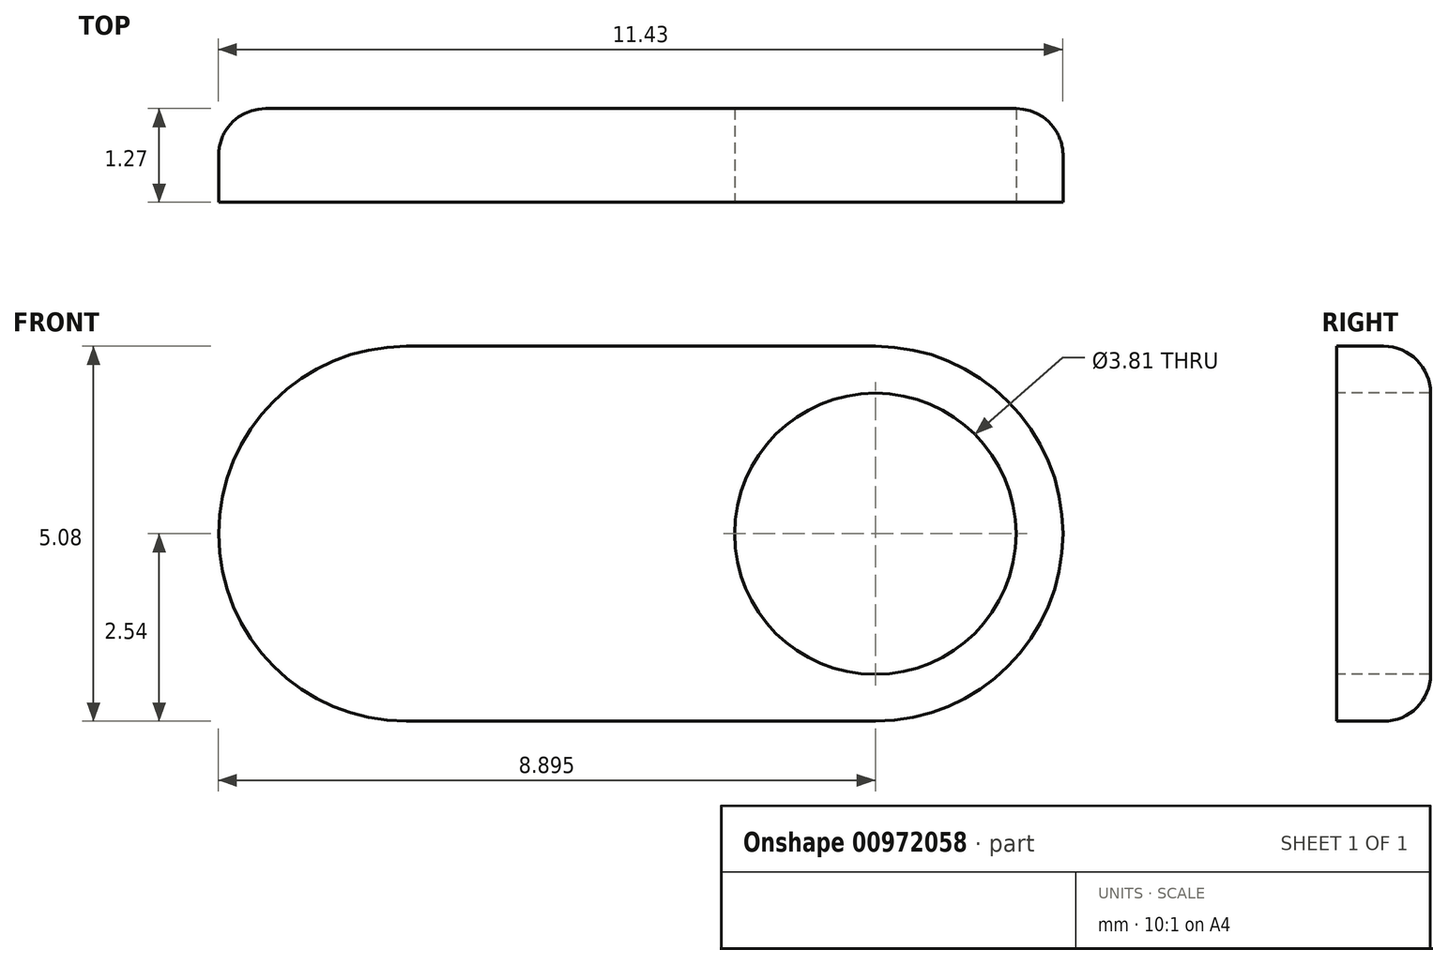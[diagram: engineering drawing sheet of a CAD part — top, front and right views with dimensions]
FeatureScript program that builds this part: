
annotation { "Feature Type Name" : "Feature", "Feature Type Description" : "" }
export const myFeature = defineFeature(function(context is Context, id is Id, definition is map)
    precondition{}
    {
        {
            var Q0;
            Q0=qCreatedBy(makeId("Front.planeOp"),FACE);
            var sketch = newSketch(context, id + "F0", { "sketchPlane" : qUnion([Q0])});
            skPoint(sketch, "E0", {"position": v(-3.17, 0) * mm});
            skPoint(sketch, "E1", {"position": v(3.18, 0) * mm});
            skCircle(sketch, "E2", {"center": v(-3.17, 0) * mm, "radius": 2.54 * mm});
            skCircle(sketch, "E3", {"center": v(3.18, 0) * mm, "radius": 2.54 * mm});
            skLineSegment(sketch, "E4", {"start": v(-3.18, 2.54) * mm, "end": v(3.18, 2.54) * mm});
            skLineSegment(sketch, "E5", {"start": v(-3.18, -2.54) * mm, "end": v(3.18, -2.54) * mm});
            skSolve(sketch);
        }
        {
            var Q0;
            Q0 = qSketchRegion(id + "F0", true);
            extrude(context, id + "F1", {"entities" : qUnion([Q0]), "depth" : 1.27 * mm, "offsetDistance" : 25.4 * mm});
        }
        {
            var Q0;
            Q0=makeQuery(id+"F1.opExtrude","CAP_EDGE",EDGE,{"disambiguationData":[OSD([sQuery(id+"F0.wireOp",EDGE,"E5")])],"isStart":true});
            fillet(context, id + "F2", {"entities" : qUnion([Q0]), "radius" : 0.64 * mm, "tangentPropagation" : true, "allowEdgeOverflow" : false});
        }
        {
            var Q0;
            Q0=makeQuery(id+"F1.opExtrude","CAP_FACE",FACE,{"disambiguationData":[OSD([sQuery(id+"F0.wireOp",EDGE,"E2"),sQuery(id+"F0.wireOp",EDGE,"E3"),sQuery(id+"F0.wireOp",EDGE,"E4"),sQuery(id+"F0.wireOp",EDGE,"E5")])],"isStart":false});
            var sketch = newSketch(context, id + "F3", { "sketchPlane" : qUnion([Q0])});
            skPoint(sketch, "E6", {"position": v(3.18, 0) * mm});
            skSolve(sketch);
        }
        {
            var Q0;
            Q0=sQuery(id+"F3.wireOp",VERTEX,"E6");
            var Q1;
            Q1=makeQuery(id+"F1.opExtrude","SWEPT_BODY",BODY,{"disambiguationData":[OSD([sQuery(id+"F0.wireOp",EDGE,"E2"),sQuery(id+"F0.wireOp",EDGE,"E3"),sQuery(id+"F0.wireOp",EDGE,"E4"),sQuery(id+"F0.wireOp",EDGE,"E5")])]});
            hole(context, id + "F4", {"style" : HoleStyle.SIMPLE, "endStyle" : HoleEndStyle.THROUGH, "holeDiameter" : 3.8 * mm, "majorDiameter" : 6.35 * mm, "isTappedThrough" : true, "tappedDepth" : 12.7 * mm, "tapClearance" : 3, "locations" : qUnion([Q0]), "scope" : qUnion([Q1])});
        }
    });
